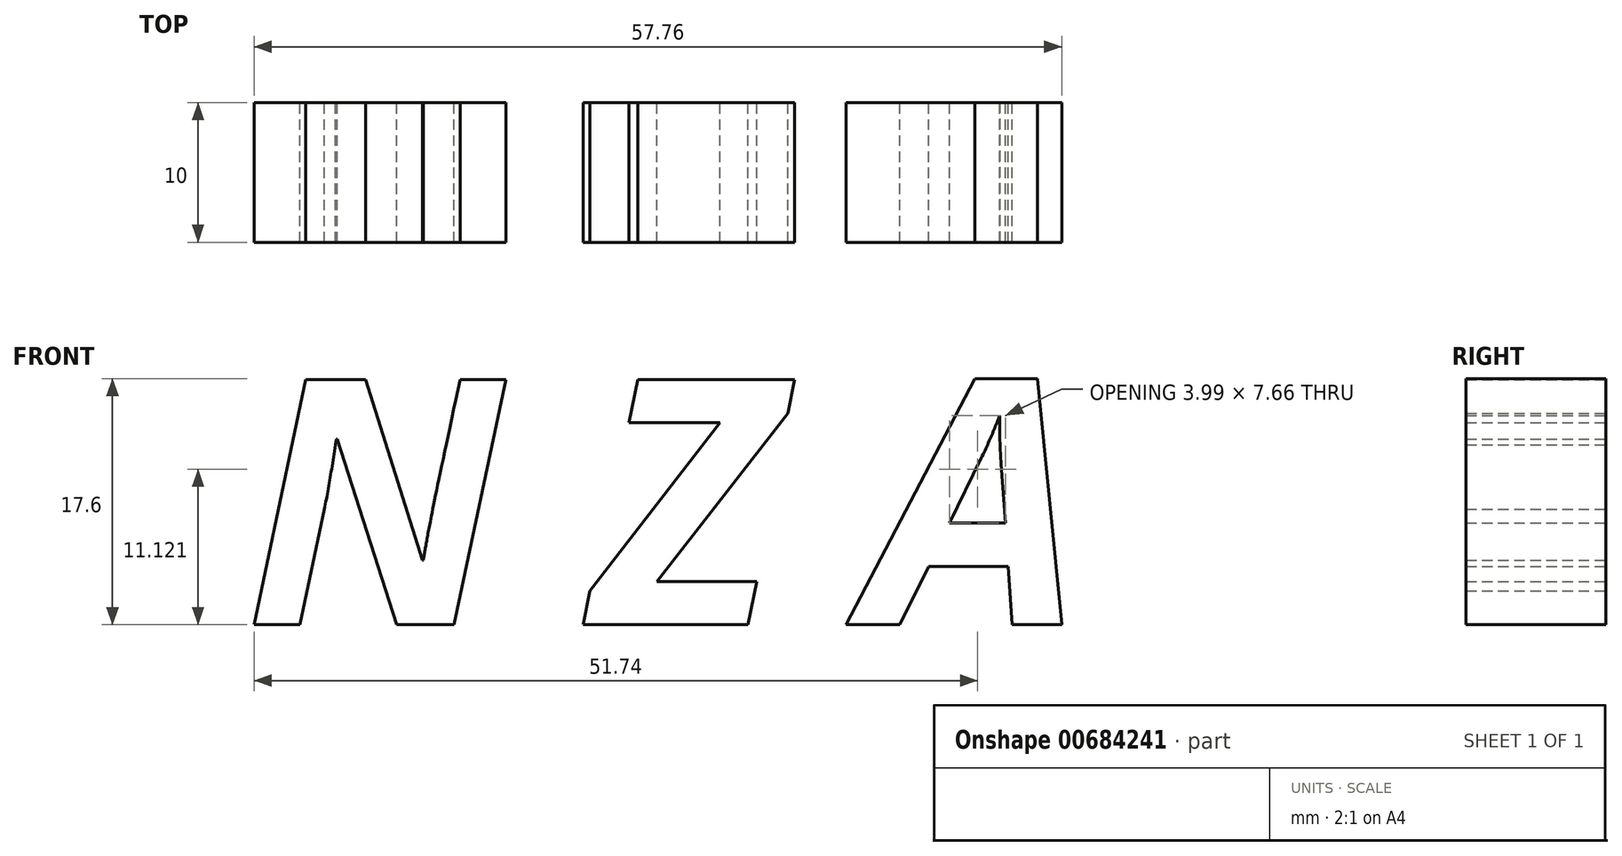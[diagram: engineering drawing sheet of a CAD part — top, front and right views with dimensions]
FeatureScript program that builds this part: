
annotation { "Feature Type Name" : "Feature", "Feature Type Description" : "" }
export const myFeature = defineFeature(function(context is Context, id is Id, definition is map)
    precondition{}
    {
        {
            var Q0;
            Q0=qCreatedBy(makeId("Front.planeOp"),FACE);
            var sketch = newSketch(context, id + "F0", { "sketchPlane" : qUnion([Q0])});
            skText(sketch, "E0", { "text": "N Z A", "fontName": "OpenSans-BoldItalic.ttf"});
            const initialGuessF0  = {"E0": [-0.00646, 0.00152, 1, 0, 0.01768]};
            skSetInitialGuess(sketch, initialGuessF0);
            skSolve(sketch);
        }
        {
            var Q0;
            Q0 = qSketchRegion(id + "F0", true);
            extrude(context, id + "F1", {"entities" : qUnion([Q0]), "depth" : 10 * mm, "offsetDistance" : 25 * mm});
        }
    });
